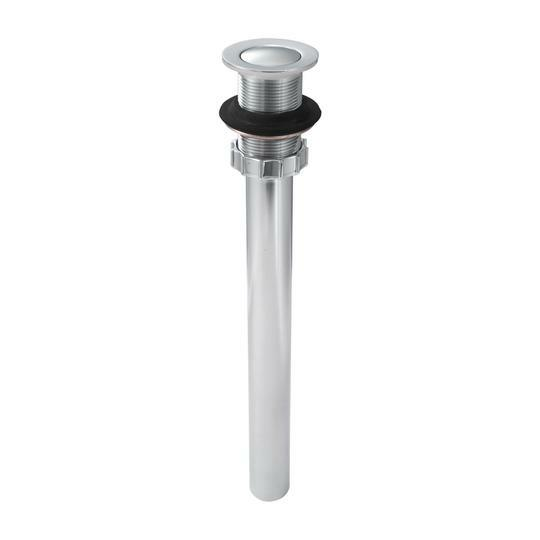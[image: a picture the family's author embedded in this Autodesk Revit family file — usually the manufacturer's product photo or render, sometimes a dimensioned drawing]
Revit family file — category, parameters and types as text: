
# Revit family: BIM_01-2906-211S
name_source: partatom
category: Aparatos sanitarios
units: mm (PartAtom-declared; Revit-internal decimal feet)

## family parameters
Activar corte en vistas = No
Anfitrión = Cara
Compartido = No
Corte con vacíos al cargar = No
Cota de conector redondo = Usar diámetro
Mantener orientación de anotación = No
Número OmniClass = 23.31.11.00
Punto de cálculo de habitación = No
Tipo de pieza = Normal

## types (1)
- 01-2906-11
    Acople = 31.8 mm  [stored 0.104331 ft]
    Alto = 377 mm  [stored 1.23688 ft]
    Caucho = Caucho
    Conexiones = Tubo para acople en tubería de 1¼”
    Conexión AC = Sí
    Conexión AF = Sí
    Conexión de residuos = No
    Conexión de ventilación = No
    Consumo aproximado a 25 psi = 27
    Date Modified = 25-08-2025
    Descripción = Desague
    Diametro = 61 mm
    Diametro Externo = 1 1/4"
    Elevación por defecto = 0 mm  [stored 0 ft]
    Fabricante = Gricol
    Garantia Especifica = 20 Años
    Goteo de Sello = 63 ml/min
    Imagen de tipo = DESAGUE LARGO PUSH METAL SIN REBOSE.jpg
    Link Ficha Tecnica = https://infotecnica.gricol.com
    Materiales del producto = Latón, Silicona, Caucho, ABS.
    Metal  Laton cromado = Metal Laton Cromado
    Modelo = 01-2906-11
    Plastico ABS Cromado = Plastico - ABS Cromado
    Product Name = Desagüe Push Metálico Sin Rebose Largo
    Referente Normativo = NTC 5302, ASME A112.18.2 / CSA B125.2
    Resistencia a Corrosión = NTC 1156, Sal Neutral
    Sitio web = https://www.gricol.com
    Temperaturas de trabajo = de 19C° A 62C°
    Tiempo de Ciclo = Domestico
    Torque de Conexioón = 20 Nm
    URL = https://www.gricol.com
    Vida Util = 100000 Ciclos

note: [stored X ft] marks values corroborated as IEEE doubles in the binary element streams (Revit-internal decimal feet)

## geometry (parser evidence)
native form markers: Blend x2, Sweep x5
no freeform markers — native parametric forms only
